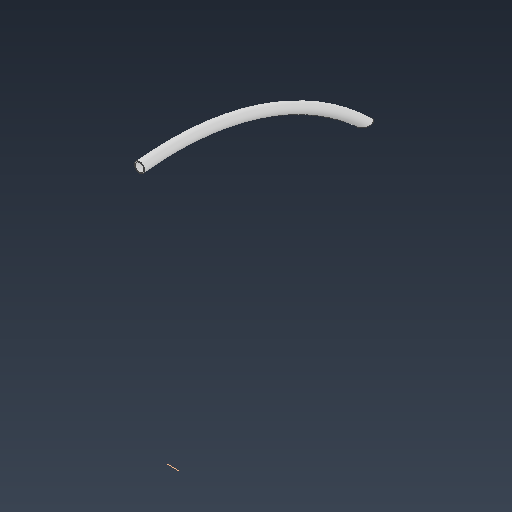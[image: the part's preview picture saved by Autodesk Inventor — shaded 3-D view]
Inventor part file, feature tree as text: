
AUTODESK INVENTOR PART (.ipt)
format: ipt  version: 2021 (Build 250183000, 183)  size: 940,032 bytes
history: native  units: mm
features: sketch x7, extrude x4, sweep x2, pattern_circular x1, fillet x1
ambient origin geometry x8: Origin, YZ Plane, XZ Plane, XY Plane, X Axis, Y Axis, Z Axis, Center Point
bodies: Solid1 (feature_tree)
feature tree (15):
  sketch  "Sketch1"  dims[d0=3300.0mm d1=1650.0mm]
  sweep  "Sweep1"
  sweep  "Sweep2"
  extrude  "Extrusion1"  Depth=50.0mm
  extrude  "Extrusion3"  Depth=1650.0mm
  pattern_circular  "Circular Pattern1"  Count=181  [1 undecoded]
  extrude  "Extrusion5"  Depth=1730.0mm
  extrude  "Extrusion6"  Depth=1730.0mm
  fillet  "Fillet1"  Radius=1730.0mm
  sketch  "Sketch2"  dims[d2=0.0mm d3=60.0mm]
  sketch  "Sketch3"  dims[d4=0.0mm d5=0.0mm d6=50.0mm]
  sketch  "Sketch4"  dims[d7=0.0mm d8=1650.0mm]
  sketch  "Sketch5"  dims[d9=0.0mm d10=0.0mm d11=1810.0mm]
  sketch  "Sketch9"  dims[d12=3460.0mm d13=1730.0mm]
  sketch  "Sketch10"  dims[d14=1200.0mm d15=1730.0mm d16=1730.0mm d17=200.0mm d18=80.0mm d19=0.0mm d20=10.0mm d21=10.0mm d22=0.5mm d25=1.0mm d26=10.0mm d27=0.0mm d28=600.0mm d29=45.0deg d38=10.0mm d39=5.0mm d40=10.0mm d41=0.0mm d42=2.0mm d43=10.0mm d44=0.0mm d45=2.0mm]
note: 1 required parameter value undecoded (feature->parameter linkage not recoverable at this tier; creation-order binding heuristic only, values carry confidence <= 0.55)
